# Revit family: ARKOSLIGHT_Bright Line Corner One Plane
name_source: partatom
category: Lighting Fixtures
units: mm (PartAtom-declared; Revit-internal decimal feet)

## family parameters
Cut with Voids When Loaded = No
Host = Face
Light Source = No
Part Type = Normal
Room Calculation Point = No
Round Connector Dimension = Use Diameter
Shared = No

## types (1)
- ARKOSLIGHT_Bright Line Corner One Plane
    ARKOSLIGHT_Apparent Load = 12 VA
    ARKOSLIGHT_Beam Angle = 110.00°
    ARKOSLIGHT_CCT = 3000 K
    ARKOSLIGHT_CRI = CRI>90
    ARKOSLIGHT_Color = Matt white
    ARKOSLIGHT_Dimming = No Dim | DALI | Push
    ARKOSLIGHT_Efficiency = 43%
    ARKOSLIGHT_Fixture Type = CUSTOM SYSTEMS
    ARKOSLIGHT_IES = A3030021 BRIGHT LINE 500 3000K CRI90.ies
    ARKOSLIGHT_IP = 20
    ARKOSLIGHT_Luminous flux = 1230 lm
    ARKOSLIGHT_Model = BRIGHT LINE
    ARKOSLIGHT_Reference = A3030071W
    ARKOSLIGHT_Series = BRIGHT LINE
    ARKOSLIGHT_Wattage = 14 W
    Apparent Load = 12 VA
    Default Elevation = 0 mm  [stored 0 ft]
    IES1 = IES1 : A3030071W - BRIGHT LINE CORNER 90º ONE PLANE A POL 3000K W
    IES2 = IES2 : A3030071W - BRIGHT LINE CORNER 90º ONE PLANE A POL 3000K W
    Manufacturer = ARKOSLIGHT
    Model = BRIGHT LINE
    URL = https://www.arkoslight.com

note: [stored X ft] marks values corroborated as IEEE doubles in the binary element streams (Revit-internal decimal feet)

## geometry (parser evidence)
native form markers: Sweep x5
no freeform markers — native parametric forms only
